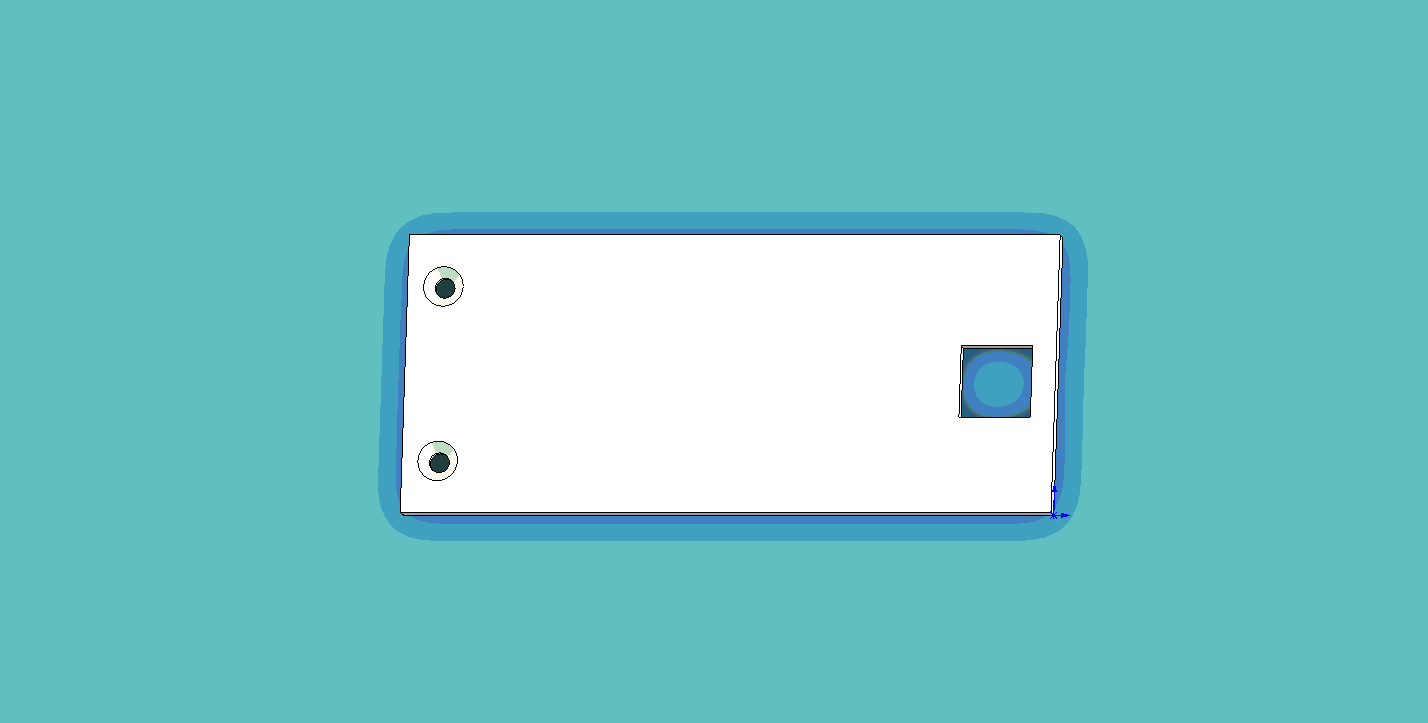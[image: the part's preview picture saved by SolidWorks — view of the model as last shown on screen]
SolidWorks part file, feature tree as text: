
SOLIDWORKS PART (.sldprt)
format: sldprt  version: not decoded by parser v0  size: 200,192 bytes
history: native  units: mm
features: plane x3, sketch x2, material x1, extrude x1, chamfer x1, cut_extrude x1 (+10 scaffold rows collapsed)
feature tree (19):
  scaffold x10  (default folders/planes/origin — collapsed)
  material  "Matériau <non spécifié>"
  plane  "Plan de face"
  plane  "Plan de dessus"
  plane  "Plan de droite"
  sketch  "Esquisse1"  dims[D3=2.5mm D1=82.0mm D2=35.0mm D4=22.0mm D5=4.5mm D6=9.0mm D7=9.0mm D8=7.5mm D9=18.5mm D10=6.5mm]
  extrude  "Extrusion1"  Depth=2mm
  chamfer  "Chanfrein1"  Distance=1.25mm Angle=45deg
  sketch  "Esquisse2"  dims[D1=0.5mm]
  cut_extrude  "Enlèv. mat.-Extru.1"  Depth=0.5mm
decode coverage: 5 of 5 modeling features carry decoded parameters
note: suppression state not decoded; provenance and decode notes live in map.json
